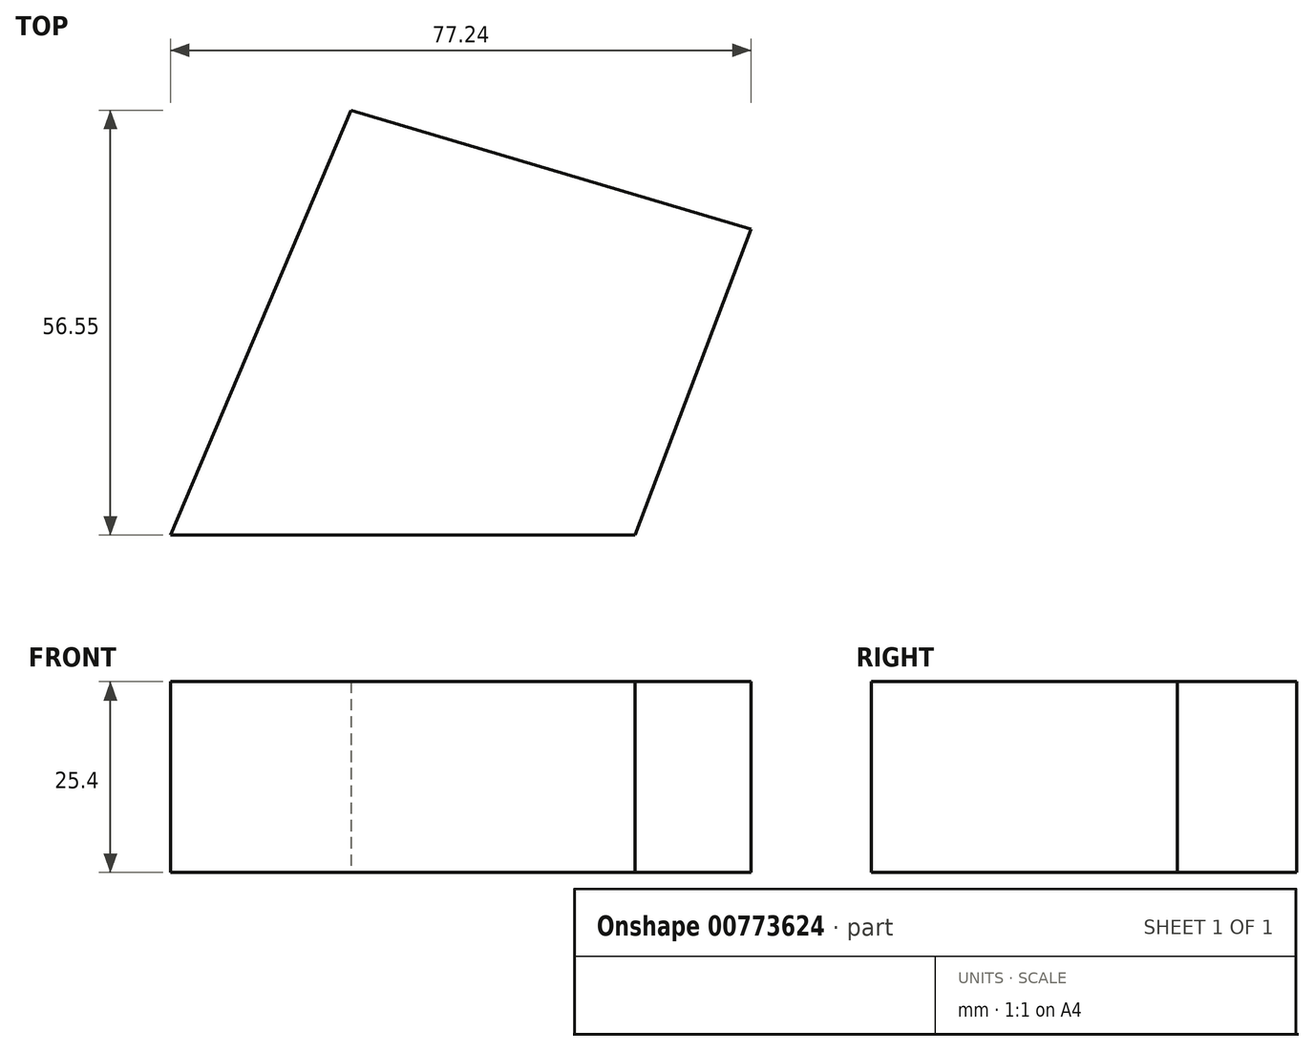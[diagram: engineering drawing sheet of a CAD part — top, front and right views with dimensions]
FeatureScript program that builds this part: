
annotation { "Feature Type Name" : "Feature", "Feature Type Description" : "" }
export const myFeature = defineFeature(function(context is Context, id is Id, definition is map)
    precondition{}
    {
        {
            var Q0;
            Q0=qCreatedBy(makeId("Top.planeOp"),FACE);
            var sketch = newSketch(context, id + "F0", { "sketchPlane" : qUnion([Q0])});
            skLineSegment(sketch, "E0", {"start": v(0, 0) * mm, "end": v(24.02, 56.55) * mm});
            skLineSegment(sketch, "E1", {"start": v(24.02, 56.55) * mm, "end": v(77.24, 40.69) * mm});
            skLineSegment(sketch, "E2", {"start": v(77.24, 40.69) * mm, "end": v(61.81, 0) * mm});
            skLineSegment(sketch, "E3", {"start": v(61.81, 0) * mm, "end": v(0, 0) * mm});
            skSolve(sketch);
        }
        {
            var Q0;
            Q0=makeQuery(id+"F0.imprint","IMPRINT",FACE,{"disambiguationData":[TD([[makeQuery(id+"F0.imprint","IMPRINT",EDGE,{"derivedFrom":sQuery(id+"F0.wireOp",EDGE,"E0")}),-1.0]])]});
            extrude(context, id + "F1", {"entities" : qUnion([Q0]), "depth" : 25.4 * mm, "offsetDistance" : 25.4 * mm});
        }
    });
